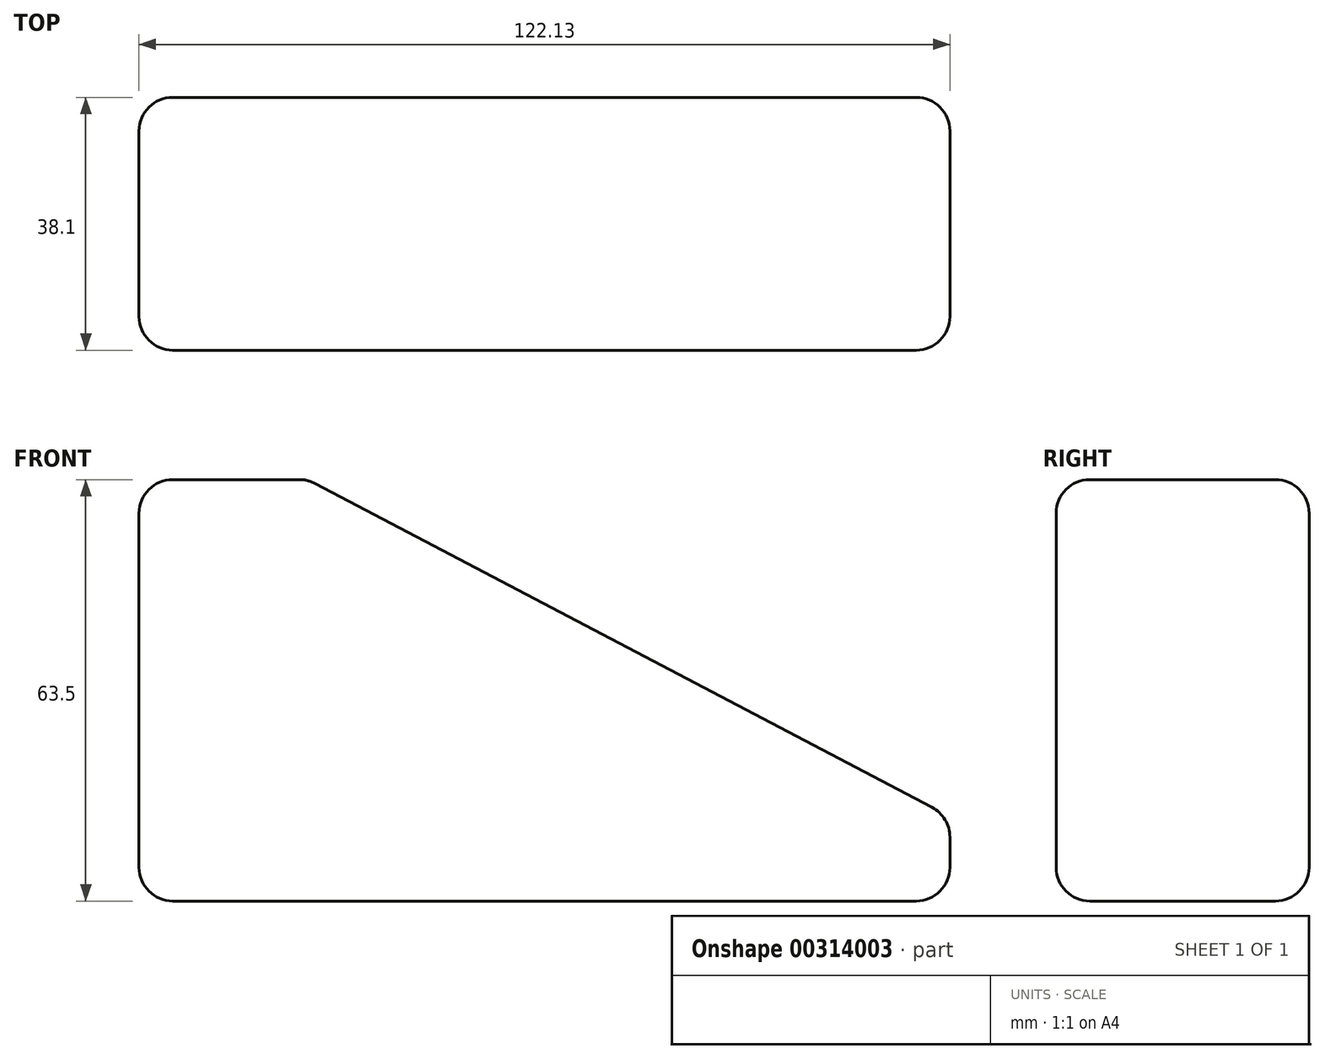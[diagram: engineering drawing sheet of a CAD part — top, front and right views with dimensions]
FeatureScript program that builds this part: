
annotation { "Feature Type Name" : "Feature", "Feature Type Description" : "" }
export const myFeature = defineFeature(function(context is Context, id is Id, definition is map)
    precondition{}
    {
        {
            var Q0;
            Q0=qCreatedBy(makeId("Front.planeOp"),FACE);
            var sketch = newSketch(context, id + "F0", { "sketchPlane" : qUnion([Q0])});
            skLineSegment(sketch, "E0", {"start": v(-58.72, 39.27) * mm, "end": v(-33.32, 39.27) * mm});
            skLineSegment(sketch, "E1", {"start": v(-58.72, 39.27) * mm, "end": v(-58.72, -24.23) * mm});
            skLineSegment(sketch, "E2", {"start": v(-58.72, -24.23) * mm, "end": v(63.4, -24.23) * mm});
            skLineSegment(sketch, "E3", {"start": v(63.4, -24.23) * mm, "end": v(63.4, -11.53) * mm});
            skLineSegment(sketch, "E4", {"start": v(-33.32, 39.27) * mm, "end": v(63.4, -11.53) * mm});
            skSolve(sketch);
        }
        {
            var Q0;
            Q0 = qSketchRegion(id + "F0", true);
            extrude(context, id + "F1", {"entities" : qUnion([Q0]), "depth" : 38.1 * mm});
        }
        {
            var Q0;
            Q0=makeQuery(id+"F1.opExtrude","SWEPT_FACE",FACE,{"disambiguationData":[OSD([sQuery(id+"F0.wireOp",EDGE,"E0")])]});
            var Q1;
            Q1=makeQuery(id+"F1.opExtrude","SWEPT_FACE",FACE,{"disambiguationData":[OSD([sQuery(id+"F0.wireOp",EDGE,"E4")])]});
            var Q2;
            Q2=makeQuery(id+"F1.opExtrude","CAP_FACE",FACE,{"disambiguationData":[OSD([sQuery(id+"F0.wireOp",EDGE,"E0"),sQuery(id+"F0.wireOp",EDGE,"E1"),sQuery(id+"F0.wireOp",EDGE,"E2"),sQuery(id+"F0.wireOp",EDGE,"E3"),sQuery(id+"F0.wireOp",EDGE,"E4")])],"isStart":false});
            var Q3;
            Q3=makeQuery(id+"F1.opExtrude","SWEPT_FACE",FACE,{"disambiguationData":[OSD([sQuery(id+"F0.wireOp",EDGE,"E3")])]});
            var Q4;
            Q4=makeQuery(id+"F1.opExtrude","CAP_FACE",FACE,{"disambiguationData":[OSD([sQuery(id+"F0.wireOp",EDGE,"E0"),sQuery(id+"F0.wireOp",EDGE,"E1"),sQuery(id+"F0.wireOp",EDGE,"E2"),sQuery(id+"F0.wireOp",EDGE,"E3"),sQuery(id+"F0.wireOp",EDGE,"E4")])],"isStart":true});
            var Q5;
            Q5=makeQuery(id+"F1.opExtrude","SWEPT_FACE",FACE,{"disambiguationData":[OSD([sQuery(id+"F0.wireOp",EDGE,"E1")])]});
            fillet(context, id + "F2", {"entities" : qUnion([Q0, Q1, Q2, Q3, Q4, Q5]), "radius" : 5.08 * mm, "tangentPropagation" : true, "allowEdgeOverflow" : false});
        }
    });
